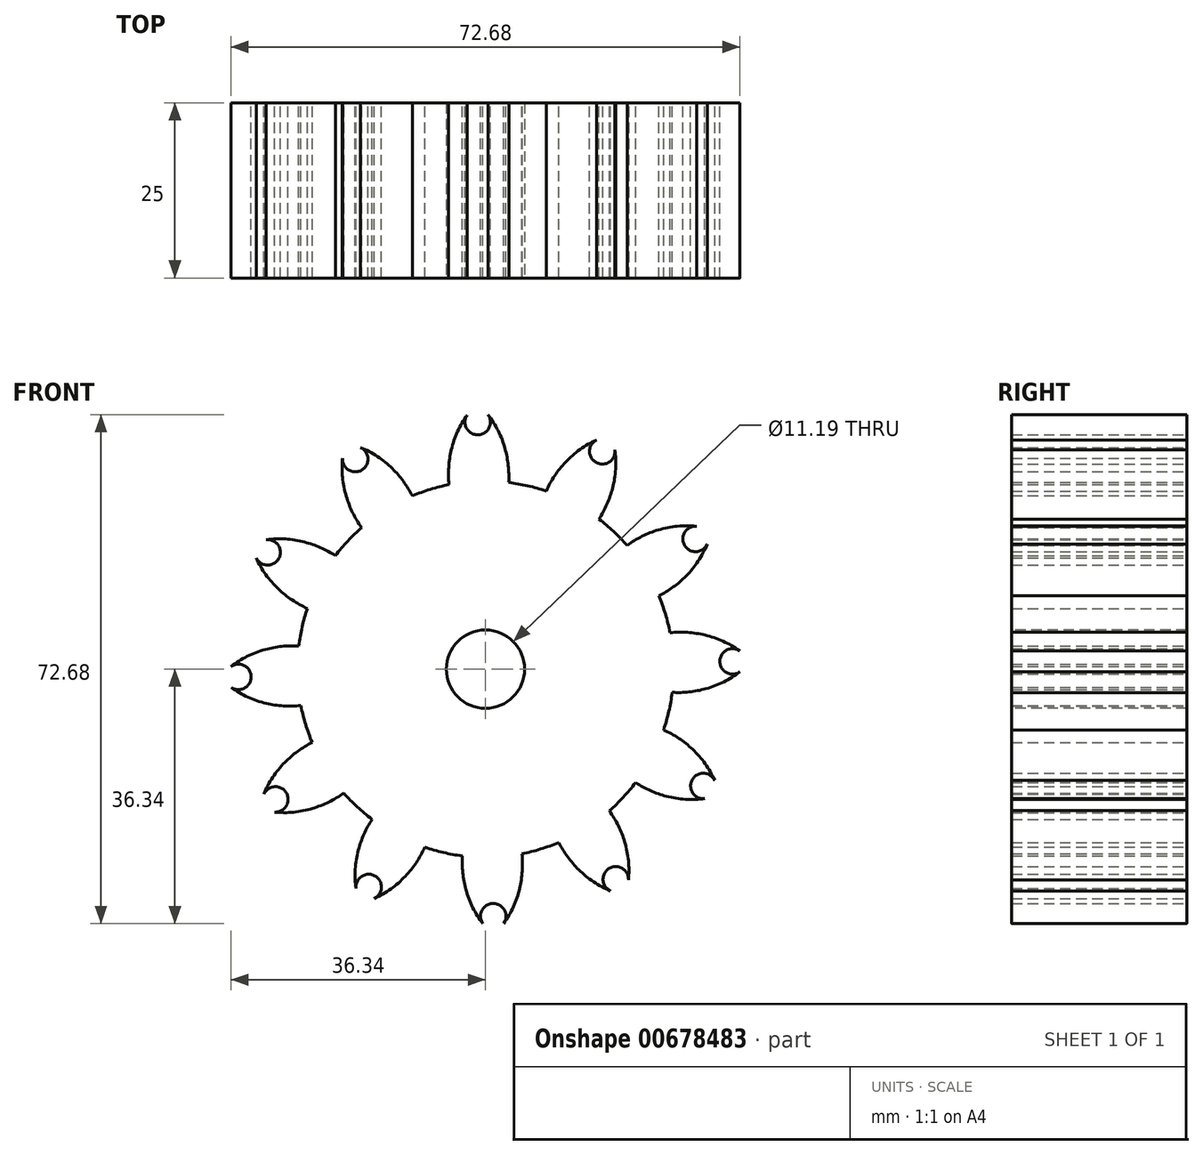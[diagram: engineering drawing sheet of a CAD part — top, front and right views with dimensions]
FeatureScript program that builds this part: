
annotation { "Feature Type Name" : "Feature", "Feature Type Description" : "" }
export const myFeature = defineFeature(function(context is Context, id is Id, definition is map)
    precondition{}
    {
        {
            var Q0;
            Q0=qCreatedBy(makeId("Front.planeOp"),FACE);
            var sketch = newSketch(context, id + "F0", { "sketchPlane" : qUnion([Q0])});
            skCircle(sketch, "E0", {"center": v(0, 0) * mm, "radius": 31.75 * mm, "construction": true});
            skCircle(sketch, "E1", {"center": v(0, 0) * mm, "radius": 29.34 * mm, "construction": true});
            skCircle(sketch, "E2", {"center": v(0, 0) * mm, "radius": 26.86 * mm});
            skArc(sketch, "E3", {"start": v(2.8, 31.45) * mm, "mid": v(1.82, 34.02) * mm, "end": v(0.36, 36.34) * mm});
            skArc(sketch, "E4", {"start": v(3.3, 26.46) * mm, "mid": v(3.26, 28.98) * mm, "end": v(2.8, 31.45) * mm});
            skArc(sketch, "E5.MirrorCS", {"start": v(-4.88, 31.31) * mm, "mid": v(-3.99, 33.91) * mm, "end": v(-2.62, 36.29) * mm});
            skArc(sketch, "E6.MirrorCS", {"start": v(-5.2, 26.31) * mm, "mid": v(-5.25, 28.83) * mm, "end": v(-4.88, 31.31) * mm});
            skArc(sketch, "E7", {"start": v(-2.62, 36.29) * mm, "mid": v(-1.08, 33.45) * mm, "end": v(0.36, 36.34) * mm});
            skSolve(sketch);
        }
        {
            var Q0;
            Q0 = qSketchRegion(id + "F0", true);
            extrude(context, id + "F1", {"entities" : qUnion([Q0]), "depth" : 25 * mm, "offsetDistance" : 25 * mm});
        }
        {
            var Q0;
            Q0=makeQuery(id+"F1.opExtrude","SWEPT_BODY",BODY,{"disambiguationData":[OSD([sQuery(id+"F0.wireOp",EDGE,"E2"),sQuery(id+"F0.wireOp",EDGE,"E3"),sQuery(id+"F0.wireOp",EDGE,"E4"),sQuery(id+"F0.wireOp",EDGE,"E5.MirrorCS"),sQuery(id+"F0.wireOp",EDGE,"E6.MirrorCS"),sQuery(id+"F0.wireOp",EDGE,"E7")])]});
            var Q1;
            Q1=makeQuery(id+"F1.opExtrude","SWEPT_FACE",FACE,{"disambiguationData":[OSD([sQuery(id+"F0.wireOp",EDGE,"E2")])]});
            circularPattern(context, id + "F2", {"operationType" : NewBodyOperationType.ADD, "entities" : qUnion([Q0]), "axis" : qUnion([Q1]), "angle" : 360 * degree, "instanceCount" : 12, "equalSpace" : true});
        }
        {
            var Q0;
            Q0=makeQuery(id+"F1.opExtrude","CAP_FACE",FACE,{"disambiguationData":[OSD([sQuery(id+"F0.wireOp",EDGE,"E2"),sQuery(id+"F0.wireOp",EDGE,"E3"),sQuery(id+"F0.wireOp",EDGE,"E4"),sQuery(id+"F0.wireOp",EDGE,"E5.MirrorCS"),sQuery(id+"F0.wireOp",EDGE,"E6.MirrorCS"),sQuery(id+"F0.wireOp",EDGE,"E7")])],"isStart":false});
            var sketch = newSketch(context, id + "F3", { "sketchPlane" : qUnion([Q0])});
            skCircle(sketch, "E8", {"center": v(0, 0) * mm, "radius": 5.6 * mm});
            skSolve(sketch);
        }
        {
            var Q0;
            Q0 = qSketchRegion(id + "F3", true);
            extrude(context, id + "F4", {"entities" : qUnion([Q0]), "operationType" : NewBodyOperationType.REMOVE, "oppositeDirection" : true, "depth" : 45.5 * mm, "offsetDistance" : 25 * mm});
        }
    });
